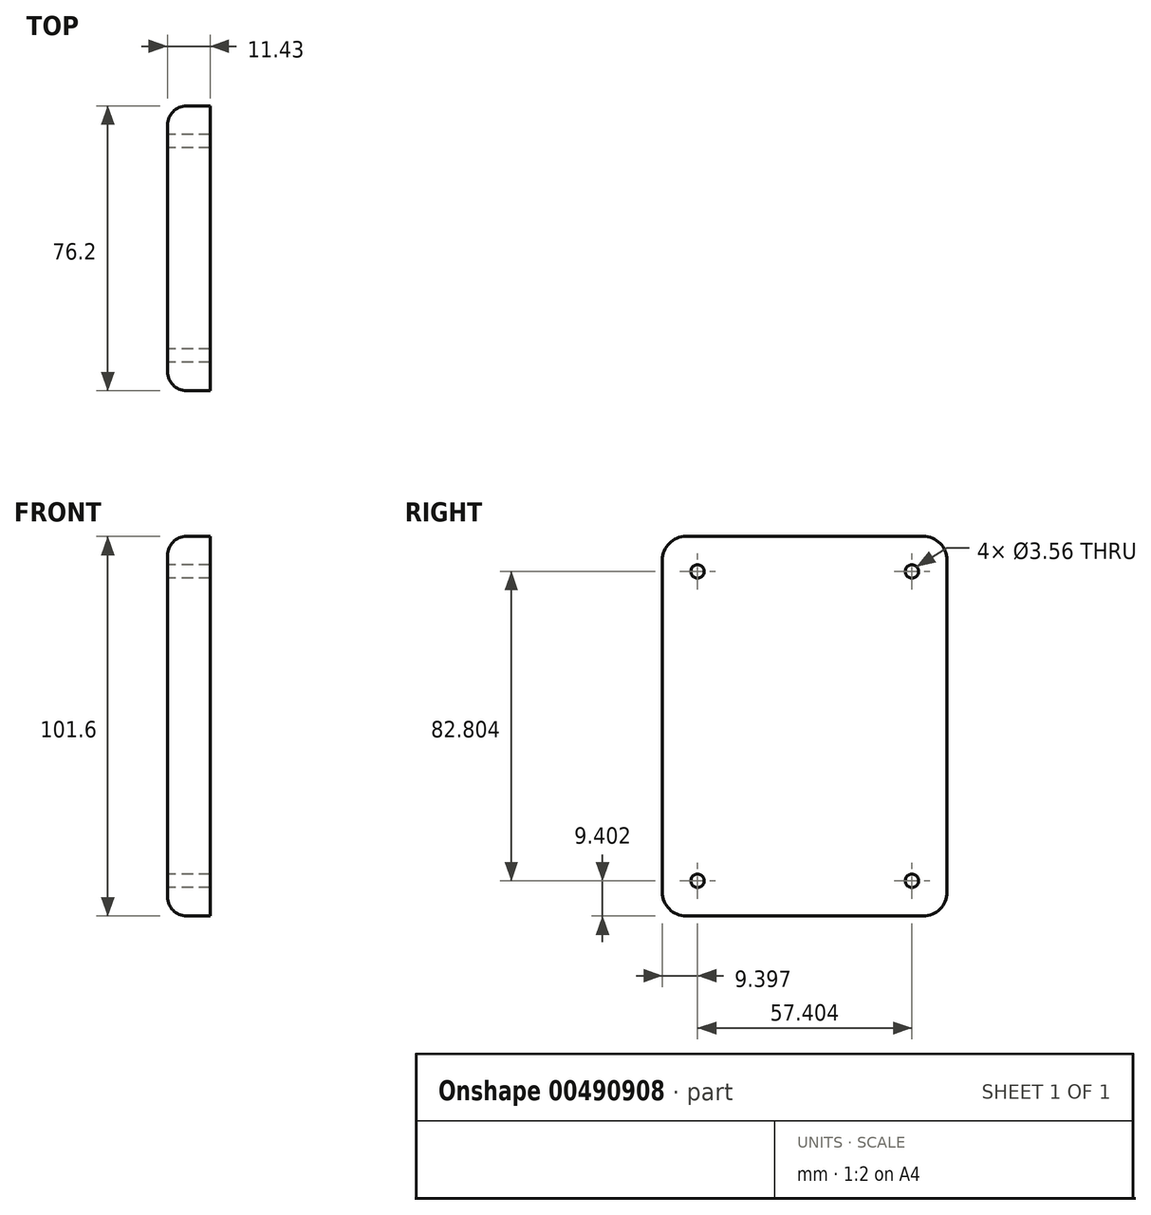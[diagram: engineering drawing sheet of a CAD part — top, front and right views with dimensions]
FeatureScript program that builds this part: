
annotation { "Feature Type Name" : "Feature", "Feature Type Description" : "" }
export const myFeature = defineFeature(function(context is Context, id is Id, definition is map)
    precondition{}
    {
        {
            var Q0;
            Q0=qCreatedBy(makeId("Right.planeOp"),FACE);
            var sketch = newSketch(context, id + "F0", { "sketchPlane" : qUnion([Q0])});
            skLineSegment(sketch, "E0.bottom", {"start": v(-34.96, 36.08) * mm, "end": v(41.24, 36.08) * mm});
            skLineSegment(sketch, "E0.top", {"start": v(-34.96, -65.52) * mm, "end": v(41.24, -65.52) * mm});
            skLineSegment(sketch, "E0.left", {"start": v(-34.96, 36.08) * mm, "end": v(-34.96, -65.52) * mm});
            skLineSegment(sketch, "E0.right", {"start": v(41.24, 36.08) * mm, "end": v(41.24, -65.52) * mm});
            skCircle(sketch, "E1", {"center": v(31.84, 26.69) * mm, "radius": 1.78 * mm});
            skCircle(sketch, "E2", {"center": v(-25.56, 26.69) * mm, "radius": 1.78 * mm});
            skCircle(sketch, "E3", {"center": v(31.84, -56.12) * mm, "radius": 1.78 * mm});
            skCircle(sketch, "E4", {"center": v(-25.56, -56.12) * mm, "radius": 1.78 * mm});
            skSolve(sketch);
        }
        {
            var Q0;
            Q0 = qSketchRegion(id + "F0", true);
            extrude(context, id + "F1", {"entities" : qUnion([Q0]), "depth" : 11.43 * mm});
        }
        {
            var Q0;
            Q0=makeQuery(id+"F1.opExtrude","SWEPT_EDGE",EDGE,{"disambiguationData":[OSD([sQuery(id+"F0.wireOp",EDGE,"E0.bottom"),sQuery(id+"F0.wireOp",EDGE,"E0.right")])]});
            var Q1;
            Q1=makeQuery(id+"F1.opExtrude","SWEPT_EDGE",EDGE,{"disambiguationData":[OSD([sQuery(id+"F0.wireOp",EDGE,"E0.top"),sQuery(id+"F0.wireOp",EDGE,"E0.right")])]});
            var Q2;
            Q2=makeQuery(id+"F1.opExtrude","SWEPT_EDGE",EDGE,{"disambiguationData":[OSD([sQuery(id+"F0.wireOp",EDGE,"E0.bottom"),sQuery(id+"F0.wireOp",EDGE,"E0.left")])]});
            var Q3;
            Q3=makeQuery(id+"F1.opExtrude","SWEPT_EDGE",EDGE,{"disambiguationData":[OSD([sQuery(id+"F0.wireOp",EDGE,"E0.top"),sQuery(id+"F0.wireOp",EDGE,"E0.left")])]});
            fillet(context, id + "F2", {"entities" : qUnion([Q0, Q1, Q2, Q3]), "radius" : 6.35 * mm, "tangentPropagation" : true, "allowEdgeOverflow" : false});
        }
        {
            var Q0;
            Q0=makeQuery(id+"F1.opExtrude","CAP_EDGE",EDGE,{"disambiguationData":[OSD([sQuery(id+"F0.wireOp",EDGE,"E0.bottom")])],"isStart":true});
            fillet(context, id + "F3", {"entities" : qUnion([Q0]), "radius" : 5.08 * mm, "tangentPropagation" : true, "allowEdgeOverflow" : false});
        }
    });
